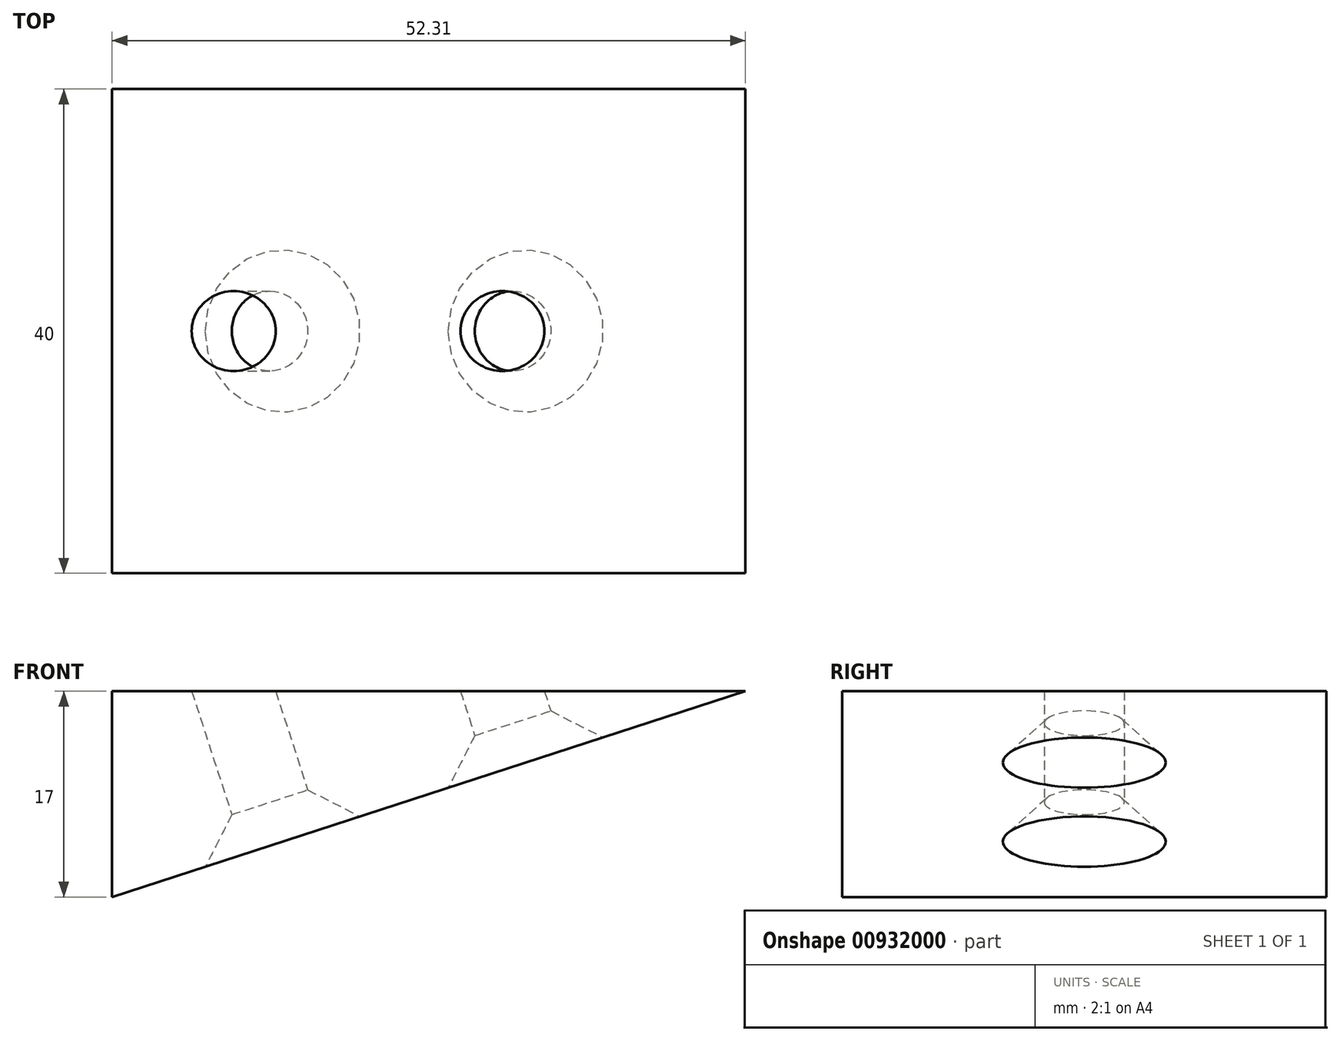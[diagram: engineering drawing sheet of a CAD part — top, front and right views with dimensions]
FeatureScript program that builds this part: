
annotation { "Feature Type Name" : "Feature", "Feature Type Description" : "" }
export const myFeature = defineFeature(function(context is Context, id is Id, definition is map)
    precondition{}
    {
        {
            var Q0;
            Q0=qCreatedBy(makeId("Front.planeOp"),FACE);
            var sketch = newSketch(context, id + "F0", { "sketchPlane" : qUnion([Q0])});
            skLineSegment(sketch, "E0", {"start": v(0, 0) * mm, "end": v(0, -17) * mm});
            skLineSegment(sketch, "E1", {"start": v(0, -17) * mm, "end": v(52.3, 0) * mm});
            skLineSegment(sketch, "E2", {"start": v(52.3, 0) * mm, "end": v(0, 0) * mm});
            skSolve(sketch);
        }
        {
            var Q0;
            Q0 = qSketchRegion(id + "F0", true);
            var Q1;
            Q1 = qSketchRegion(id + "FFCYCf5ateXSujs_1", true);
            extrude(context, id + "F1", {"entities" : qUnion([Q0, Q1]), "depth" : 40 * mm, "offsetDistance" : 25 * mm});
        }
        {
            var Q0;
            Q0=makeQuery(id+"F1.opExtrude","SWEPT_FACE",FACE,{"disambiguationData":[OSD([sQuery(id+"F0.wireOp",EDGE,"E1")])]});
            var sketch = newSketch(context, id + "F2", { "sketchPlane" : qUnion([Q0])});
            skLineSegment(sketch, "E3", {"start": v(-5.25, 20) * mm, "end": v(49.75, 20) * mm, "construction": true});
            skPoint(sketch, "E4", {"position": v(9.55, 20) * mm});
            skPoint(sketch, "E5", {"position": v(30.66, 20) * mm});
            skSolve(sketch);
        }
        {
            var Q0;
            Q0=sQuery(id+"F2.wireOp",VERTEX,"E4");
            var Q1;
            Q1=sQuery(id+"F2.wireOp",VERTEX,"E5");
            var Q2;
            Q2=makeQuery(id+"F1.opExtrude","SWEPT_BODY",BODY,{"disambiguationData":[OSD([sQuery(id+"F0.wireOp",EDGE,"E0"),sQuery(id+"F0.wireOp",EDGE,"E1"),sQuery(id+"F0.wireOp",EDGE,"E2")])]});
            hole(context, id + "F3", {"style" : HoleStyle.C_SINK, "endStyle" : HoleEndStyle.THROUGH, "standardTappedOrClearance" : lookupTablePath({ "fit" : "Normal", "standard" : "ISO", "size" : "M6", "type" : "Clearance" }), "standardBlindInLast" : lookupTablePath({ "fit" : "Normal", "standard" : "ISO", "engagement" : "75%", "pitch" : "1 mm", "size" : "M6", "type" : "Clearance & tapped" }), "holeDiameter" : 6.6 * mm, "cSinkDiameter" : 13.44 * mm, "cSinkAngle" : 90 * degree, "majorDiameter" : 5 * mm, "isTappedThrough" : true, "tappedDepth" : 12 * mm, "tapClearance" : 3, "locations" : qUnion([Q0, Q1]), "scope" : qUnion([Q2])});
        }
    });
